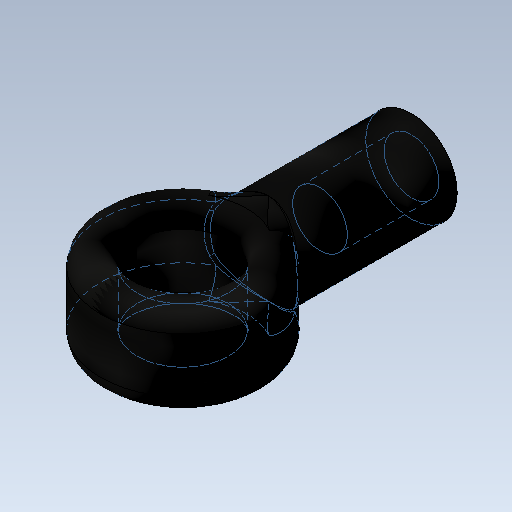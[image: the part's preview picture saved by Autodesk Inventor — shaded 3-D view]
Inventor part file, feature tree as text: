
AUTODESK INVENTOR PART (.ipt)
format: ipt  version: 2020 (Build 240168000, 168)  size: 244,224 bytes
history: native  units: mm
features: extrude x3, sketch x3, fillet x2, other x1
ambient origin geometry x8: Origin, YZ Plane, XZ Plane, XY Plane, X Axis, Y Axis, Z Axis, Center Point
bodies: Body1 (feature_tree)
feature tree (9):
  other  "ソリッド1"
  extrude  "押し出し1"  Depth=5.0mm
  extrude  "押し出し2"  Depth=8.5mm TaperAngle=0.0deg
  extrude  "押し出し3"  Depth=5.0mm
  fillet  "フィレット1"  Radius=9.0mm
  fillet  "フィレット2"  Radius=4.0mm
  sketch  "スケッチ1"
  sketch  "スケッチ2"
  sketch  "スケッチ3"
